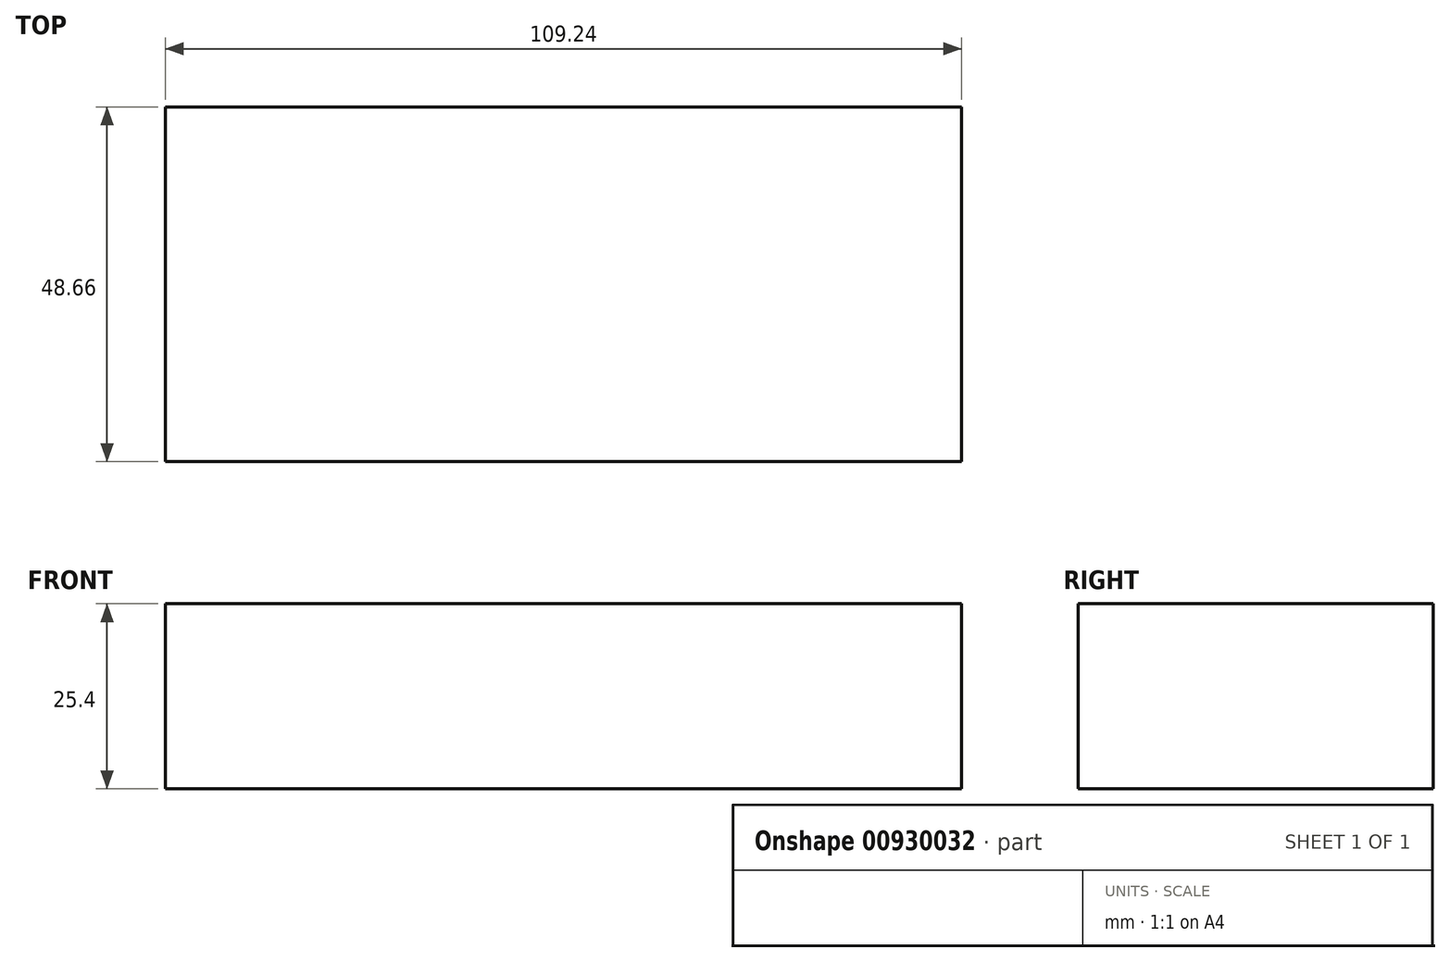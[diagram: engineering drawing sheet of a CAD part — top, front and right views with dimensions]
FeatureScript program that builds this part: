
annotation { "Feature Type Name" : "Feature", "Feature Type Description" : "" }
export const myFeature = defineFeature(function(context is Context, id is Id, definition is map)
    precondition{}
    {
        {
            var Q0;
            Q0=qCreatedBy(makeId("Top.planeOp"),FACE);
            var sketch = newSketch(context, id + "F0", { "sketchPlane" : qUnion([Q0])});
            skLineSegment(sketch, "E0.bottom", {"start": v(-54.69, 24.86) * mm, "end": v(54.55, 24.86) * mm});
            skLineSegment(sketch, "E0.top", {"start": v(-54.69, -23.8) * mm, "end": v(54.55, -23.8) * mm});
            skLineSegment(sketch, "E0.left", {"start": v(-54.69, 24.86) * mm, "end": v(-54.69, -23.8) * mm});
            skLineSegment(sketch, "E0.right", {"start": v(54.55, 24.86) * mm, "end": v(54.55, -23.8) * mm});
            skSolve(sketch);
        }
        {
            var Q0;
            Q0=makeQuery(id+"F0.imprint","IMPRINT",FACE,{"disambiguationData":[TD([[makeQuery(id+"F0.imprint","IMPRINT",EDGE,{"derivedFrom":sQuery(id+"F0.wireOp",EDGE,"E0.bottom")}),-1.0]])]});
            extrude(context, id + "F1", {"entities" : qUnion([Q0]), "depth" : 25.4 * mm, "offsetDistance" : 25.4 * mm});
        }
    });
